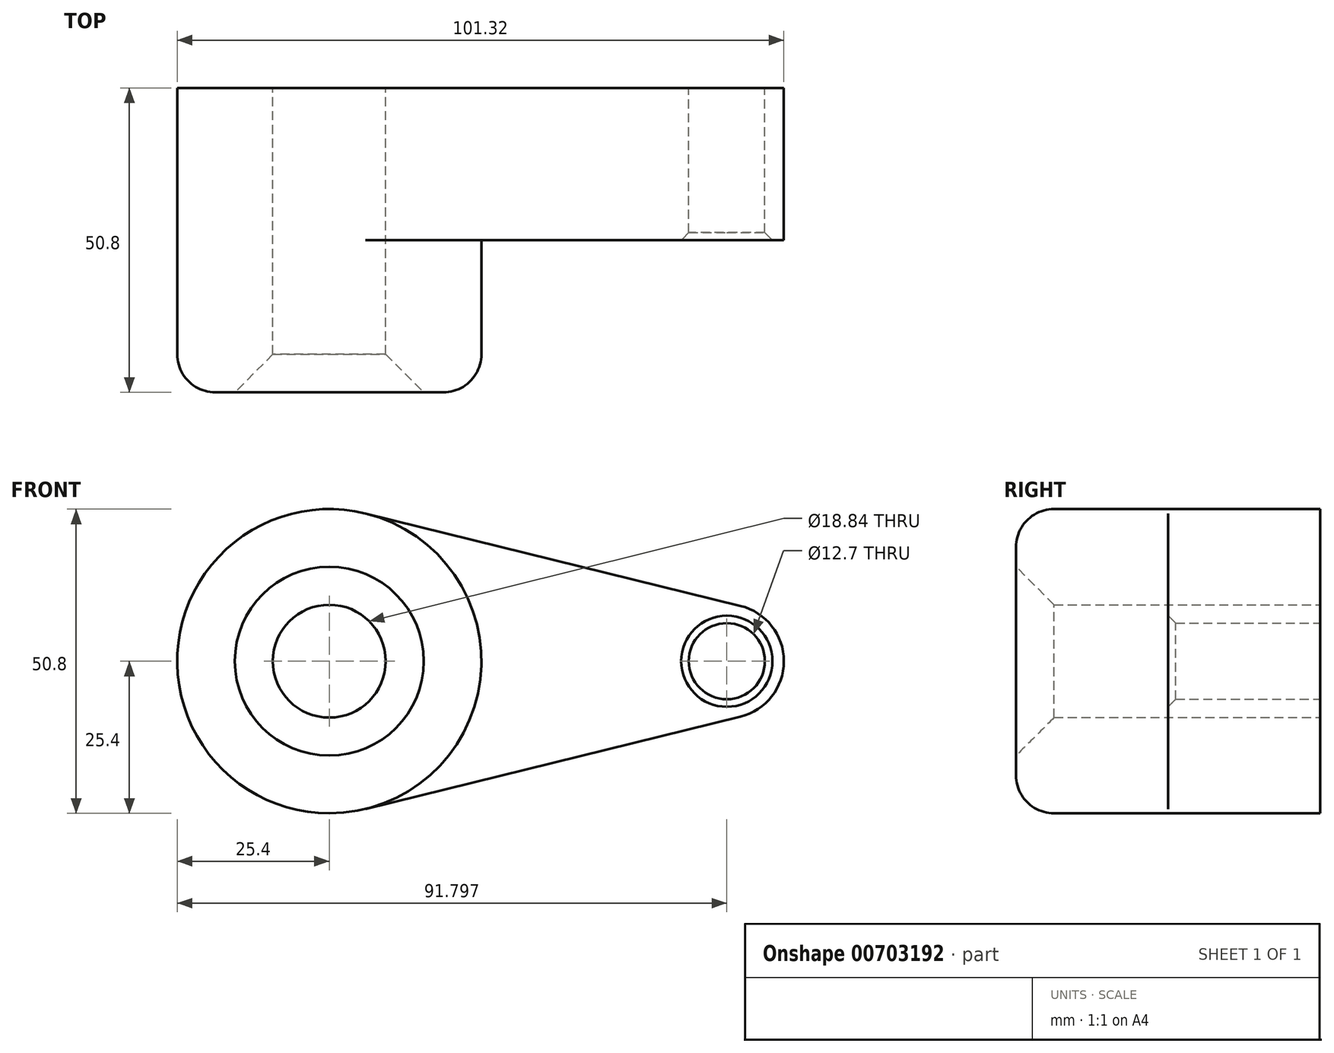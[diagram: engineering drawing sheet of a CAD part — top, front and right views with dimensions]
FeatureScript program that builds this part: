
annotation { "Feature Type Name" : "Feature", "Feature Type Description" : "" }
export const myFeature = defineFeature(function(context is Context, id is Id, definition is map)
    precondition{}
    {
        {
            var Q0;
            Q0=qCreatedBy(makeId("Front.planeOp"),FACE);
            var sketch = newSketch(context, id + "F0", { "sketchPlane" : qUnion([Q0])});
            skCircle(sketch, "E0", {"center": v(0, 0) * mm, "radius": 25.4 * mm});
            skCircle(sketch, "E1", {"center": v(66.4, 0) * mm, "radius": 9.53 * mm});
            skLineSegment(sketch, "E2", {"start": v(6.07, 24.66) * mm, "end": v(68.67, 9.25) * mm});
            skLineSegment(sketch, "E3", {"start": v(6.07, -24.66) * mm, "end": v(68.67, -9.25) * mm});
            skCircle(sketch, "E4", {"center": v(0, 0) * mm, "radius": 9.42 * mm});
            skCircle(sketch, "E5", {"center": v(66.4, 0) * mm, "radius": 6.35 * mm});
            skSolve(sketch);
        }
        {
            var Q0;
            Q0=makeQuery(id+"F0.imprint","IMPRINT",FACE,{"disambiguationData":[TD([[makeQuery(id+"F0.imprint","IMPRINT",EDGE,{"derivedFrom":sQuery(id+"F0.wireOp",EDGE,"E4")}),-1.0]])]});
            var Q1;
            {var subQ0=sQuery(id+"F0.wireOp",EDGE,"E2");Q1=makeQuery(id+"F0.imprint","IMPRINT",FACE,{"disambiguationData":[TD([[makeQuery(id+"F0.imprint","IMPRINT",EDGE,{"derivedFrom":subQ0}),-1.0]])]});}
            var Q2;
            Q2=makeQuery(id+"F0.imprint","IMPRINT",FACE,{"disambiguationData":[TD([[makeQuery(id+"F0.imprint","IMPRINT",EDGE,{"derivedFrom":sQuery(id+"F0.wireOp",EDGE,"E5")}),-1.0]])]});
            extrude(context, id + "F1", {"entities" : qUnion([Q0, Q1, Q2]), "depth" : 25.4 * mm, "offsetDistance" : 25.4 * mm});
        }
        {
            var Q0;
            Q0=makeQuery(id+"F0.imprint","IMPRINT",FACE,{"disambiguationData":[TD([[makeQuery(id+"F0.imprint","IMPRINT",EDGE,{"derivedFrom":sQuery(id+"F0.wireOp",EDGE,"E4")}),-1.0]])]});
            extrude(context, id + "F2", {"entities" : qUnion([Q0]), "operationType" : NewBodyOperationType.ADD, "depth" : 50.8 * mm, "offsetDistance" : 25.4 * mm});
        }
        {
            var Q0;
            Q0=makeQuery(id+"F2.opExtrude","CAP_EDGE",EDGE,{"disambiguationData":[OSD([sQuery(id+"F0.wireOp",EDGE,"E0")])],"isStart":false});
            fillet(context, id + "F3", {"entities" : qUnion([Q0]), "radius" : 6.35 * mm, "tangentPropagation" : true, "allowEdgeOverflow" : false});
        }
        {
            var Q0;
            Q0=makeQuery(id+"F2.opExtrude","CAP_EDGE",EDGE,{"disambiguationData":[OSD([sQuery(id+"F0.wireOp",EDGE,"E4")])],"isStart":false});
            chamfer(context, id + "F4", {"entities" : qUnion([Q0]), "width" : 6.35 * mm, "tangentPropagation" : true});
        }
        {
            var Q0;
            Q0=makeQuery(id+"F1.opExtrude","CAP_EDGE",EDGE,{"disambiguationData":[OSD([sQuery(id+"F0.wireOp",EDGE,"E5")])],"isStart":false});
            chamfer(context, id + "F5", {"entities" : qUnion([Q0]), "width" : 1.27 * mm, "tangentPropagation" : true});
        }
    });
